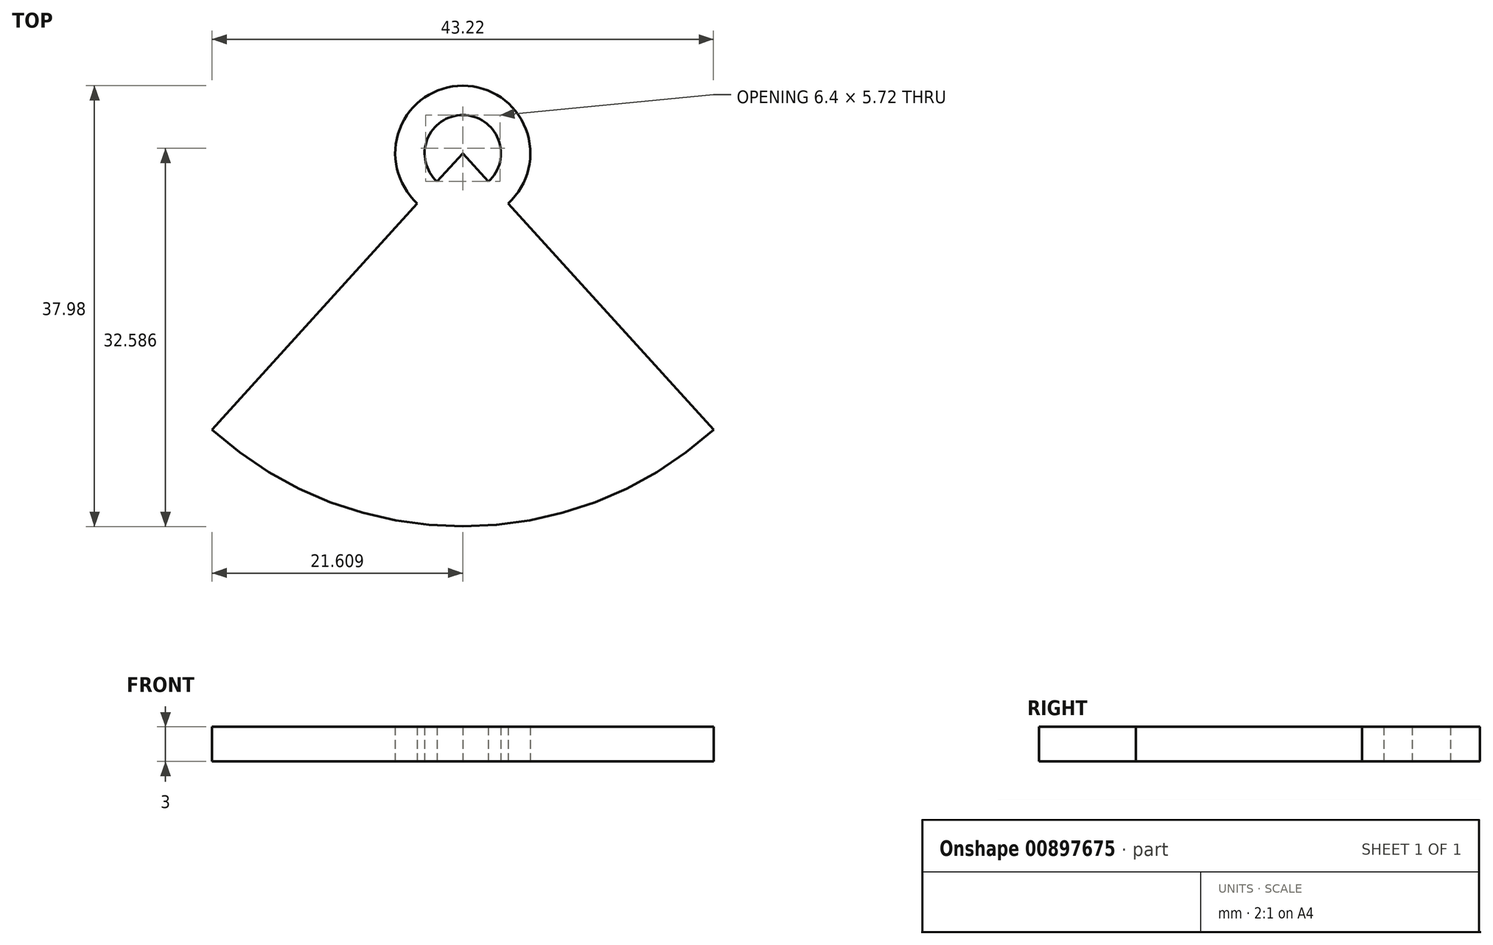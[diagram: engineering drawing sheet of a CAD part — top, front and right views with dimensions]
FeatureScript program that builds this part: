
annotation { "Feature Type Name" : "Feature", "Feature Type Description" : "" }
export const myFeature = defineFeature(function(context is Context, id is Id, definition is map)
    precondition{}
    {
        {
            var Q0;
            Q0=qCreatedBy(makeId("Top.planeOp"),FACE);
            var sketch = newSketch(context, id + "F0", { "sketchPlane" : qUnion([Q0])});
            skArc(sketch, "E0", {"start": v(-21.5, 0) * mm, "mid": v(0.1, -8.35) * mm, "end": v(21.72, 0) * mm});
            skLineSegment(sketch, "E1", {"start": v(0.1, 23.8) * mm, "end": v(-21.5, 0) * mm});
            skLineSegment(sketch, "E2", {"start": v(0.1, 23.8) * mm, "end": v(21.72, 0) * mm});
            skArc(sketch, "E3", {"start": v(-15.83, 0) * mm, "mid": v(0.1, -4.84) * mm, "end": v(16.05, 0) * mm});
            skLineSegment(sketch, "E4", {"start": v(0.1, 23.8) * mm, "end": v(-15.83, 0) * mm});
            skLineSegment(sketch, "E5", {"start": v(16.05, 0) * mm, "end": v(0.1, 23.8) * mm});
            skArc(sketch, "E6", {"start": v(-10.6, 0) * mm, "mid": v(0.39, -2.26) * mm, "end": v(11.36, 0) * mm});
            skLineSegment(sketch, "E7", {"start": v(0.1, 23.8) * mm, "end": v(-10.6, 0) * mm});
            skLineSegment(sketch, "E8", {"start": v(0.1, 23.8) * mm, "end": v(11.36, 0) * mm});
            skArc(sketch, "E9", {"start": v(4.02, 19.5) * mm, "mid": v(0.1, 29.63) * mm, "end": v(-3.8, 19.5) * mm});
            skArc(sketch, "E10", {"start": v(2.32, 21.37) * mm, "mid": v(0.1, 27.1) * mm, "end": v(-2.1, 21.37) * mm});
            skSolve(sketch);
        }
        {
            var Q0;
            Q0=makeQuery(id+"F0.imprint","IMPRINT",FACE,{"disambiguationData":[TD([[makeQuery(id+"F0.imprint","IMPRINT",EDGE,{"derivedFrom":sQuery(id+"F0.wireOp",EDGE,"E3")}),1.0]])]});
            var Q1;
            Q1=makeQuery(id+"F0.imprint","IMPRINT",FACE,{"disambiguationData":[TD([[makeQuery(id+"F0.imprint","IMPRINT",EDGE,{"derivedFrom":sQuery(id+"F0.wireOp",EDGE,"E6")}),1.0]])]});
            var Q2;
            Q2=makeQuery(id+"F0.imprint","IMPRINT",FACE,{"disambiguationData":[TD([[makeQuery(id+"F0.imprint","IMPRINT",EDGE,{"derivedFrom":sQuery(id+"F0.wireOp",EDGE,"E0")}),1.0]])]});
            extrude(context, id + "F1", {"entities" : qUnion([Q0, Q1, Q2]), "depth" : 3 * mm, "offsetDistance" : 25.4 * mm});
        }
        {
            var Q0;
            Q0=sQuery(id+"F0.wireOp",EDGE,"E6");
            extrude(context, id + "F2", {"bodyType" : ToolBodyType.SURFACE, "surfaceEntities" : qUnion([Q0]), "oppositeDirection" : true, "depth" : 2 * mm, "offsetDistance" : 25.4 * mm});
        }
        {
            var Q0;
            Q0=sQuery(id+"F0.wireOp",EDGE,"E7");
            var Q1;
            Q1=sQuery(id+"F0.wireOp",EDGE,"E8");
            extrude(context, id + "F3", {"bodyType" : ToolBodyType.SURFACE, "surfaceEntities" : qUnion([Q0, Q1]), "oppositeDirection" : true, "depth" : 2 * mm, "offsetDistance" : 25.4 * mm});
        }
        {
            var Q0;
            Q0=sQuery(id+"F0.wireOp",EDGE,"E4");
            var Q1;
            Q1=sQuery(id+"F0.wireOp",EDGE,"E3");
            var Q2;
            Q2=sQuery(id+"F0.wireOp",EDGE,"E5");
            extrude(context, id + "F4", {"bodyType" : ToolBodyType.SURFACE, "surfaceEntities" : qUnion([Q0, Q1, Q2]), "oppositeDirection" : true, "depth" : 2 * mm, "offsetDistance" : 25.4 * mm});
        }
        {
            var Q0;
            Q0=sQuery(id+"F0.wireOp",EDGE,"E2");
            var Q1;
            Q1=sQuery(id+"F0.wireOp",EDGE,"E0");
            var Q2;
            Q2=sQuery(id+"F0.wireOp",EDGE,"E1");
            extrude(context, id + "F5", {"bodyType" : ToolBodyType.SURFACE, "surfaceEntities" : qUnion([Q0, Q1, Q2]), "oppositeDirection" : true, "depth" : 2 * mm, "offsetDistance" : 25.4 * mm});
        }
        {
            var Q0;
            {var subQ0=sQuery(id+"F0.wireOp",EDGE,"E9");Q0=makeQuery(id+"F0.imprint","IMPRINT",FACE,{"disambiguationData":[TD([[makeQuery(id+"F0.imprint","IMPRINT",EDGE,{"derivedFrom":subQ0}),1.0]])]});}
            extrude(context, id + "F6", {"entities" : qUnion([Q0]), "operationType" : NewBodyOperationType.ADD, "depth" : 3 * mm, "offsetDistance" : 25.4 * mm});
        }
    });
